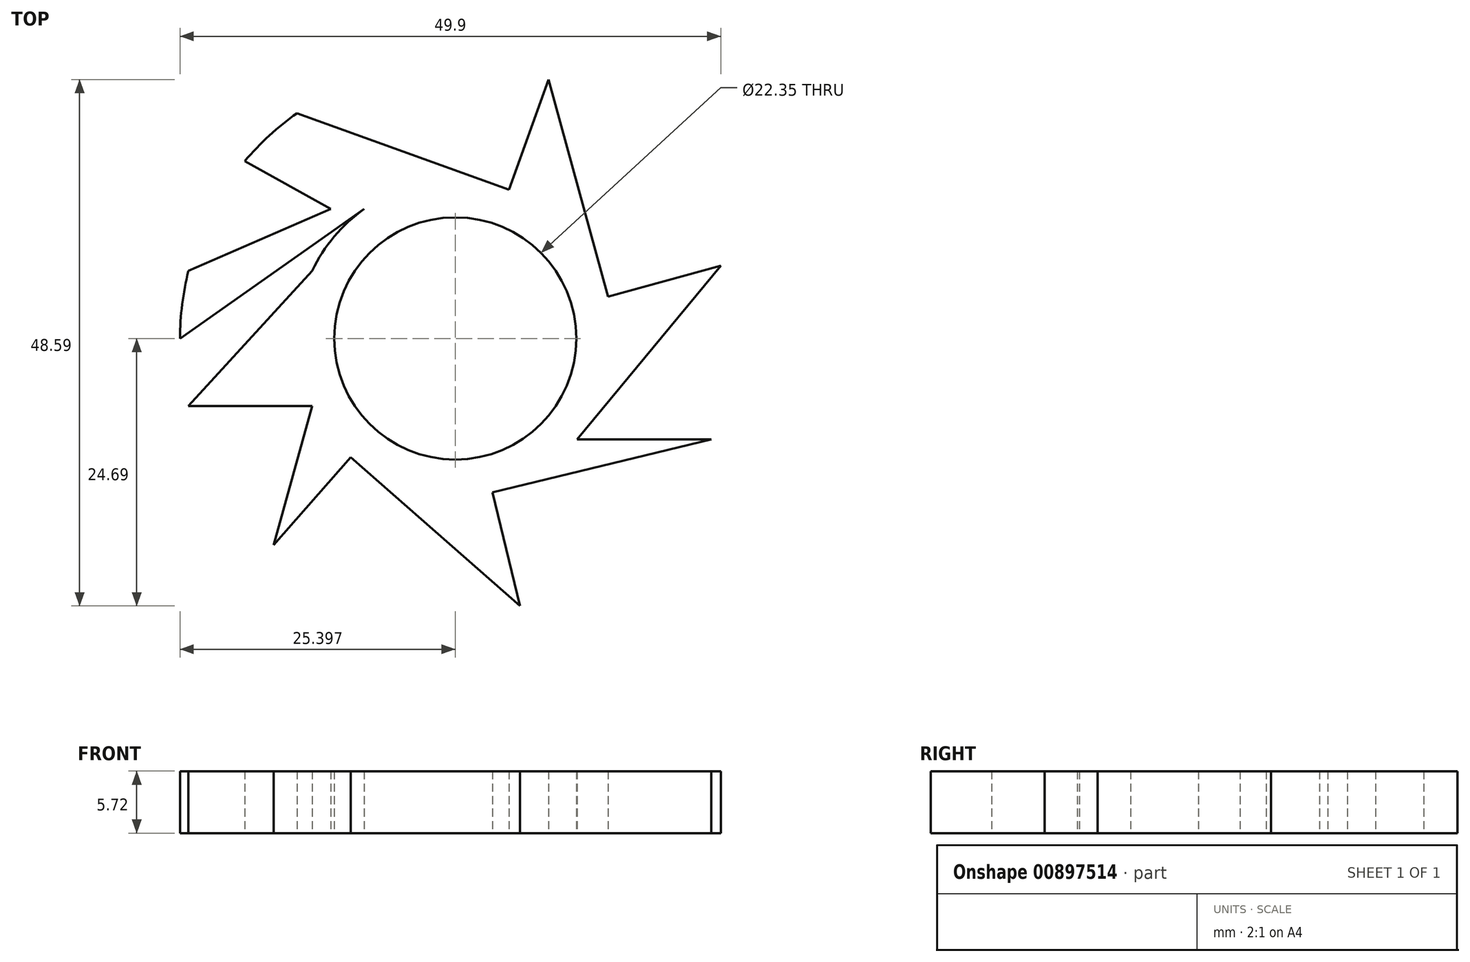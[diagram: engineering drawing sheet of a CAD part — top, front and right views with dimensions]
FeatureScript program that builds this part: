
annotation { "Feature Type Name" : "Feature", "Feature Type Description" : "" }
export const myFeature = defineFeature(function(context is Context, id is Id, definition is map)
    precondition{}
    {
        {
            var Q0;
            Q0=qCreatedBy(makeId("Top.planeOp"),FACE);
            var sketch = newSketch(context, id + "F0", { "sketchPlane" : qUnion([Q0])});
            skCircle(sketch, "E0", {"center": v(-5.54, 0) * mm, "radius": 11.18 * mm});
            skCircle(sketch, "E1", {"center": v(-5.54, 0) * mm, "radius": 14.6 * mm});
            skCircle(sketch, "E2", {"center": v(-5.54, 0) * mm, "radius": 25.4 * mm});
            skLineSegment(sketch, "E3", {"start": v(-23.4, 0) * mm, "end": v(-30.94, 0) * mm});
            skLineSegment(sketch, "E4", {"start": v(-30.94, 0) * mm, "end": v(-13.94, 11.95) * mm});
            skLineSegment(sketch, "E5", {"start": v(-13.94, 11.95) * mm, "end": v(-20.15, 20.78) * mm});
            skLineSegment(sketch, "E6", {"start": v(-20.15, 20.78) * mm, "end": v(-0.6, 13.74) * mm});
            skLineSegment(sketch, "E7", {"start": v(-0.6, 13.74) * mm, "end": v(3.06, 23.9) * mm});
            skLineSegment(sketch, "E8", {"start": v(3.06, 23.9) * mm, "end": v(8.54, 3.85) * mm});
            skLineSegment(sketch, "E9", {"start": v(8.54, 3.85) * mm, "end": v(18.96, 6.7) * mm});
            skLineSegment(sketch, "E10", {"start": v(18.96, 6.7) * mm, "end": v(5.7, -9.3) * mm});
            skLineSegment(sketch, "E11", {"start": v(5.7, -9.3) * mm, "end": v(18.09, -9.3) * mm});
            skLineSegment(sketch, "E12", {"start": v(18.09, -9.3) * mm, "end": v(-2.1, -14.2) * mm});
            skPoint(sketch, "E13.end.orphan", {"position": v(-5.54, -25.4) * mm});
            skLineSegment(sketch, "E14", {"start": v(-2.1, -14.2) * mm, "end": v(0.43, -24.69) * mm});
            skLineSegment(sketch, "E15", {"start": v(0.43, -24.69) * mm, "end": v(-15.18, -10.97) * mm});
            skLineSegment(sketch, "E16", {"start": v(-15.18, -10.97) * mm, "end": v(-22.3, -19.08) * mm});
            skLineSegment(sketch, "E17", {"start": v(-22.3, -19.08) * mm, "end": v(-18.75, -6.25) * mm});
            skPoint(sketch, "E17.endSnap0", {"position": v(-18.75, -15.03) * mm});
            skLineSegment(sketch, "E18", {"start": v(-18.75, -6.25) * mm, "end": v(-30.16, -6.25) * mm});
            skLineSegment(sketch, "E19", {"start": v(-30.16, -6.25) * mm, "end": v(-18.75, 6.25) * mm});
            skLineSegment(sketch, "E20", {"start": v(-18.75, 6.25) * mm, "end": v(-30.94, 0) * mm});
            skLineSegment(sketch, "E21", {"start": v(2.33, -14.2) * mm, "end": v(4.54, -23.31) * mm});
            skLineSegment(sketch, "E22", {"start": v(2.33, -14.2) * mm, "end": v(17.58, -10.5) * mm});
            skLineSegment(sketch, "E23", {"start": v(17.58, 10.5) * mm, "end": v(9.96, 8.42) * mm});
            skPoint(sketch, "E23.endSnap0", {"position": v(9.96, -12.35) * mm});
            skLineSegment(sketch, "E24", {"start": v(9.96, 8.42) * mm, "end": v(6.08, 22.58) * mm});
            skLineSegment(sketch, "E25", {"start": v(-0.6, 24.91) * mm, "end": v(-2.79, 18.82) * mm});
            skPoint(sketch, "E25.endSnap0", {"position": v(1.23, 18.82) * mm});
            skLineSegment(sketch, "E26", {"start": v(-2.79, 18.82) * mm, "end": v(-15.46, 23.38) * mm});
            skLineSegment(sketch, "E27", {"start": v(-17.04, 11.95) * mm, "end": v(-24.97, 16.37) * mm});
            skPoint(sketch, "E27.startSnap0", {"position": v(-17.04, 16.37) * mm});
            skPoint(sketch, "E27.endSnap0", {"position": v(-17.04, 16.37) * mm});
            skLineSegment(sketch, "E28", {"start": v(-17.04, 11.95) * mm, "end": v(-30.16, 6.25) * mm});
            skLineSegment(sketch, "E29", {"start": v(12.33, -6.23) * mm, "end": v(19.08, -6.23) * mm});
            skPoint(sketch, "E29.startSnap0", {"position": v(12.33, -1.3) * mm});
            skLineSegment(sketch, "E30", {"start": v(12.33, -6.23) * mm, "end": v(19.71, 2.69) * mm});
            skLineSegment(sketch, "E31", {"start": v(-14.77, -15.03) * mm, "end": v(-18.75, -21.7) * mm});
            skLineSegment(sketch, "E32", {"start": v(-14.77, -15.03) * mm, "end": v(-2.43, -25.2) * mm});
            skCircle(sketch, "E33", {"center": v(-5.54, 0) * mm, "radius": 27.5 * mm});
            skSolve(sketch);
        }
        {
            var Q0;
            {var subQ0=sQuery(id+"F0.wireOp",EDGE,"E16");Q0=makeQuery(id+"F0.imprint","IMPRINT",FACE,{"disambiguationData":[TD([[makeQuery(id+"F0.imprint","IMPRINT",EDGE,{"derivedFrom":subQ0}),-1.0]])]});}
            var Q1;
            {var subQ0=sQuery(id+"F0.wireOp",EDGE,"E18");Q1=makeQuery(id+"F0.imprint","IMPRINT",FACE,{"disambiguationData":[TD([[makeQuery(id+"F0.imprint","IMPRINT",EDGE,{"derivedFrom":subQ0}),-1.0]])]});}
            var Q2;
            {var subQ0=sQuery(id+"F0.wireOp",EDGE,"E14");Q2=makeQuery(id+"F0.imprint","IMPRINT",FACE,{"disambiguationData":[TD([[makeQuery(id+"F0.imprint","IMPRINT",EDGE,{"derivedFrom":subQ0}),-1.0]])]});}
            var Q3;
            {var subQ0=sQuery(id+"F0.wireOp",EDGE,"E11");Q3=makeQuery(id+"F0.imprint","IMPRINT",FACE,{"disambiguationData":[TD([[makeQuery(id+"F0.imprint","IMPRINT",EDGE,{"derivedFrom":subQ0}),-1.0]])]});}
            var Q4;
            {var subQ0=sQuery(id+"F0.wireOp",EDGE,"E7");Q4=makeQuery(id+"F0.imprint","IMPRINT",FACE,{"disambiguationData":[TD([[makeQuery(id+"F0.imprint","IMPRINT",EDGE,{"derivedFrom":subQ0}),-1.0]])]});}
            var Q5;
            {var subQ0=sQuery(id+"F0.wireOp",EDGE,"E5");Q5=makeQuery(id+"F0.imprint","IMPRINT",FACE,{"disambiguationData":[TD([[makeQuery(id+"F0.imprint","IMPRINT",EDGE,{"derivedFrom":subQ0}),-1.0]])]});}
            var Q6;
            {var subQ0=sQuery(id+"F0.wireOp",EDGE,"E9");Q6=makeQuery(id+"F0.imprint","IMPRINT",FACE,{"disambiguationData":[TD([[makeQuery(id+"F0.imprint","IMPRINT",EDGE,{"derivedFrom":subQ0}),-1.0]])]});}
            var Q7;
            {var subQ0=sQuery(id+"F0.wireOp",EDGE,"E4");Q7=makeQuery(id+"F0.imprint","IMPRINT",FACE,{"disambiguationData":[TD([[makeQuery(id+"F0.imprint","IMPRINT",EDGE,{"derivedFrom":subQ0}),1.0]])]});}
            var Q8;
            Q8=makeQuery(id+"F0.imprint","IMPRINT",FACE,{"disambiguationData":[TD([[makeQuery(id+"F0.imprint","IMPRINT",EDGE,{"derivedFrom":sQuery(id+"F0.wireOp",EDGE,"E0")}),-1.0]])]});
            extrude(context, id + "F1", {"entities" : qUnion([Q0, Q1, Q2, Q3, Q4, Q5, Q6, Q7, Q8]), "depth" : 5.7 * mm, "offsetDistance" : 25.4 * mm});
        }
    });
